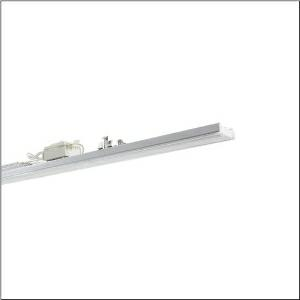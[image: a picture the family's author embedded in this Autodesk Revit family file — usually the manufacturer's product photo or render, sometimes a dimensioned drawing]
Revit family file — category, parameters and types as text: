
# Revit family: licross_11_recessed_ho_51tl1emn4d5s
name_source: partatom
category: Lighting Fixtures
units: mm (PartAtom-declared; Revit-internal decimal feet)

## family parameters
Cut with Voids When Loaded = No
Host = Face
Light Source = No
Part Type = Normal
Room Calculation Point = No
Round Connector Dimension = Use Diameter
Shared = No

## types (1)
- --- (1 x LED, 13740 lm, 74.5 W, 4000K)
    Apparent Load = 75 VA
    CIE Flux Codes = 85 95 99 100 100
    Color Rendering = 80
    Color Temperature = 4000K
    Default Elevation = 1800 mm
    Description = Licross 11 Recessed HO, luminaire insert, of sheet steel, coil coated, white, length: 1.500mm, width: 66mm, height: 67mm, LED rated luminous flux: 13.740lm, light colour: 840, SDCM (Standard Deviation of Colour Matching)MacAdam ≤ 2 SDCM (initial), control gear: ON/OFF Multilumen, with plug, 3-pole, with phase selection, mains connection: 220..240V, AC, 50/60Hz, rated input power: 75W, internal wiring halogen-free, primary light control with lens, of plastic, primary optical cover: cover, of PMMA, light emission: direct distribution, primary light characteristic: symmetric, protection rating (complete): IP40, insulation class (complete): insulation class I (protective earthing), certification: CE, ENEC, VDE, UKCA, protection symbol: D if used in an environment without relevant dust loads with corresponding accessories, impact resistance: IK06, permissible ambient temperature for indoor applications: -35..+35°C, corresponds to IFS (International Featured Standards) requirements for safety and quality in the food industry, reducing of maximum allowable ambient temperature of 5°C with ceiling mounting, The light source and the operating device comply with the requirements of the Ecodesign Regulation (EU) 2019/2020 and are replaceable in accordance with this regulation, packaging unit: 1 piece
    Height = 58 mm
    Lamp = 1 x LED
    Lamp Light Flux = 13740 lm
    Lamp Power = 74.5 W
    Lamp count = 1
    Length = 1500 mm
    Luminous efficacy = 184 lm/W
    Manufacturer = Siteco
    ModVariant = No
    Model = 51TL1EMN4D5S
    Mounting Place = Ceiling
    Mounting Type = Pendant
    Number of Poles = 1
    OnlyDefault = Yes
    Power Factor = 1
    Product Name = Licross 11 Recessed HO
    Product group = luminaire insert | ceiling pendant
    ProductGroupID = 901
    Protection Class = Protection class I
    Protection Degree = IP 40
    RLX_Detail_Level = 1
    RLX_Emergency_Light_Flux = 0 lm
    RLX_Emergency_Type = 0
    RLX_Emergency_Type_DB = No
    RlxData = <blob elided: 22629 chars, md5=cf9ac104>
    Socket = socket
    Standby Power = 0 W
    System Light Flux = 13740 lm
    System Power = 75 W
    Type Comments = factory setting: luminous flux: 100 % | (A | C | E) | 174 mA
    Type Image = l_1296930.jpg
    URL = http://relux.com
    VarID = @adj_089289
    Voltage = 0 V
    Weight = 0.00 kg
    Width = 66 mm

## geometry (parser evidence)
native form markers: Blend x4, Sweep x12
no freeform markers — native parametric forms only
